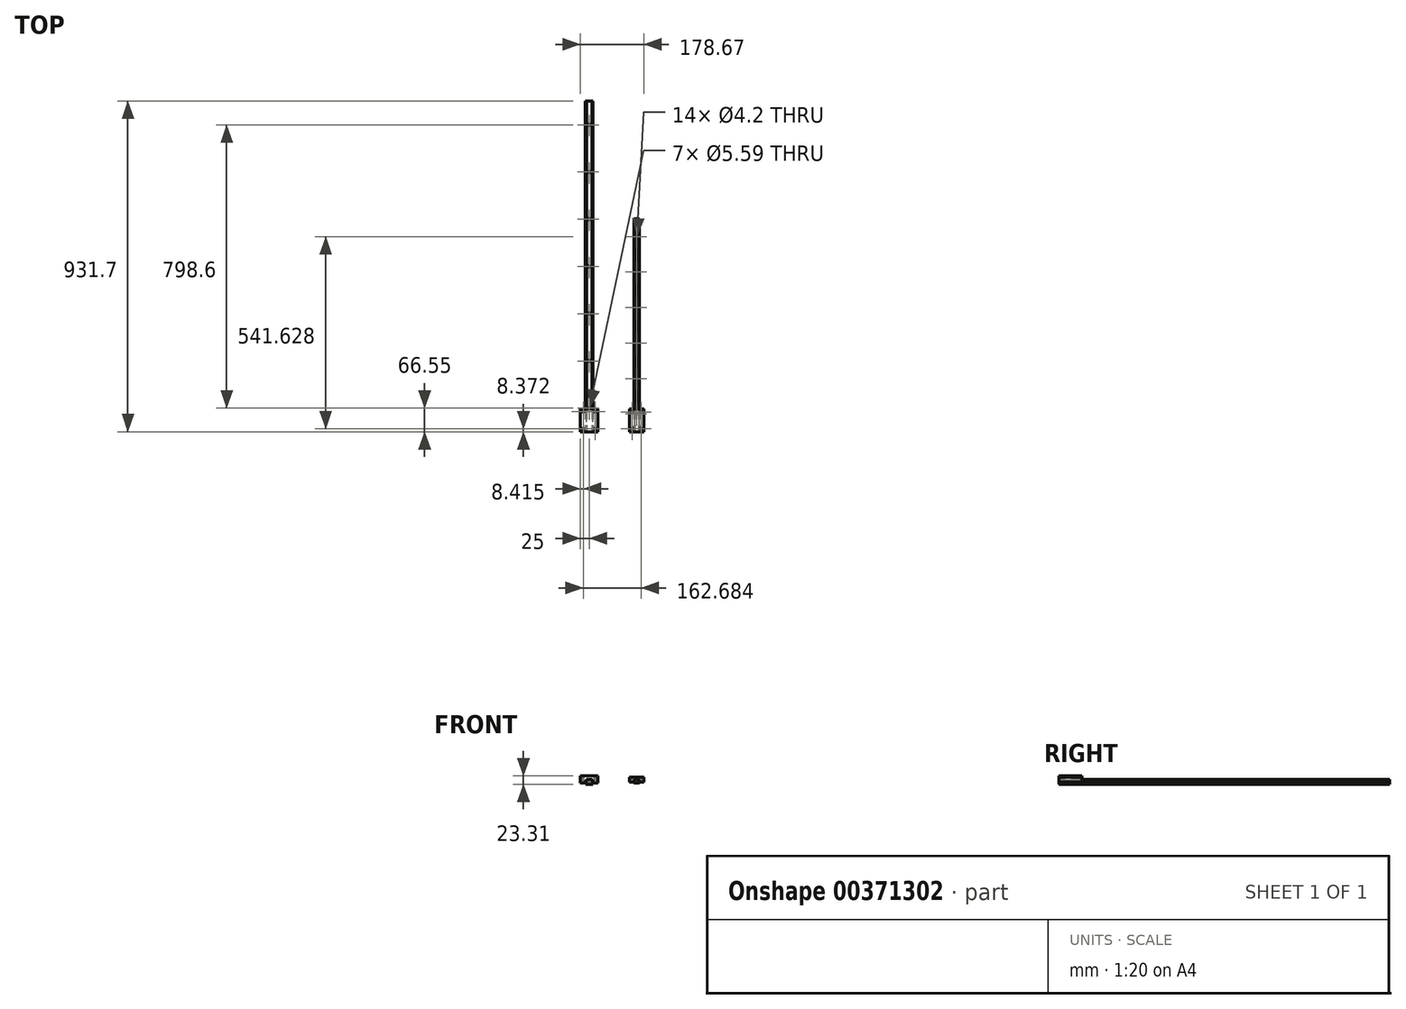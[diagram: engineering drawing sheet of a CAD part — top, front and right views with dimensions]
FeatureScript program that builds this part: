
annotation { "Feature Type Name" : "Feature", "Feature Type Description" : "" }
export const myFeature = defineFeature(function(context is Context, id is Id, definition is map)
    precondition{}
    {
        {
            var Q0;
            Q0=qCreatedBy(makeId("Front.planeOp"),FACE);
            var sketch = newSketch(context, id + "F0", { "sketchPlane" : qUnion([Q0])});
            skLineSegment(sketch, "E0", {"start": v(47.88, 76.41) * mm, "end": v(58.88, 76.41) * mm});
            skLineSegment(sketch, "E1", {"start": v(47.88, 76.41) * mm, "end": v(47.88, 75.41) * mm});
            skLineSegment(sketch, "E2", {"start": v(46.88, 74.41) * mm, "end": v(45.88, 74.41) * mm});
            skLineSegment(sketch, "E3", {"start": v(45.88, 74.41) * mm, "end": v(45.88, 73.91) * mm});
            skLineSegment(sketch, "E4", {"start": v(45.88, 73.91) * mm, "end": v(45.38, 73.91) * mm});
            skPoint(sketch, "E5.visualSharp", {"position": v(47.88, 74.41) * mm});
            skArc(sketch, "E5.filletArc", {"start": v(46.88, 74.41) * mm, "mid": v(47.59, 74.7) * mm, "end": v(47.88, 75.41) * mm});
            skLineSegment(sketch, "E6", {"start": v(45.38, 73.91) * mm, "end": v(45.38, 73.41) * mm});
            skLineSegment(sketch, "E7", {"start": v(45.38, 73.41) * mm, "end": v(45.88, 73.41) * mm});
            skLineSegment(sketch, "E8", {"start": v(45.88, 69.41) * mm, "end": v(45.88, 66.41) * mm});
            skArc(sketch, "E9", {"start": v(45.88, 69.41) * mm, "mid": v(46.83, 71.41) * mm, "end": v(45.88, 73.41) * mm});
            skLineSegment(sketch, "E10", {"start": v(53.38, 80.8) * mm, "end": v(53.38, 84.76) * mm, "construction": true});
            skPoint(sketch, "E10.startSnap0", {"position": v(53.38, 76.41) * mm});
            skLineSegment(sketch, "E11.MirrorCS", {"start": v(58.88, 76.41) * mm, "end": v(58.88, 75.41) * mm});
            skArc(sketch, "E12.MirrorCS", {"start": v(59.88, 74.41) * mm, "mid": v(59.17, 74.7) * mm, "end": v(58.88, 75.41) * mm});
            skLineSegment(sketch, "E13.MirrorCS", {"start": v(59.88, 74.41) * mm, "end": v(60.88, 74.41) * mm});
            skLineSegment(sketch, "E14.MirrorCS", {"start": v(60.88, 74.41) * mm, "end": v(60.88, 73.91) * mm});
            skLineSegment(sketch, "E15.MirrorCS", {"start": v(60.88, 73.91) * mm, "end": v(61.38, 73.91) * mm});
            skLineSegment(sketch, "E16.MirrorCS", {"start": v(61.38, 73.91) * mm, "end": v(61.38, 73.41) * mm});
            skLineSegment(sketch, "E17.MirrorCS", {"start": v(61.38, 73.41) * mm, "end": v(60.88, 73.41) * mm});
            skArc(sketch, "E18.MirrorCS", {"start": v(60.88, 69.41) * mm, "mid": v(59.93, 71.41) * mm, "end": v(60.88, 73.41) * mm});
            skLineSegment(sketch, "E19.MirrorCS", {"start": v(60.88, 69.41) * mm, "end": v(60.88, 66.41) * mm});
            skLineSegment(sketch, "E20", {"start": v(45.88, 66.41) * mm, "end": v(60.88, 66.41) * mm});
            skLineSegment(sketch, "E21", {"start": v(120.22, 88.93) * mm, "end": v(120.22, 157.33) * mm, "construction": true});
            skLineSegment(sketch, "E22.MirrorCS", {"start": v(194.55, 73.91) * mm, "end": v(195.05, 73.91) * mm});
            skLineSegment(sketch, "E23.MirrorCS", {"start": v(194.55, 74.41) * mm, "end": v(194.55, 73.91) * mm});
            skArc(sketch, "E24.MirrorCS", {"start": v(193.55, 74.41) * mm, "mid": v(192.85, 74.7) * mm, "end": v(192.55, 75.41) * mm});
            skLineSegment(sketch, "E25.MirrorCS", {"start": v(195.05, 73.41) * mm, "end": v(194.55, 73.41) * mm});
            skLineSegment(sketch, "E26.MirrorCS", {"start": v(179.55, 74.41) * mm, "end": v(179.55, 73.91) * mm});
            skLineSegment(sketch, "E27.MirrorCS", {"start": v(179.55, 73.91) * mm, "end": v(179.05, 73.91) * mm});
            skLineSegment(sketch, "E28.MirrorCS", {"start": v(193.55, 74.41) * mm, "end": v(194.55, 74.41) * mm});
            skLineSegment(sketch, "E29.MirrorCS", {"start": v(195.05, 73.91) * mm, "end": v(195.05, 73.41) * mm});
            skArc(sketch, "E30.MirrorCS", {"start": v(180.55, 74.41) * mm, "mid": v(181.26, 74.7) * mm, "end": v(181.55, 75.41) * mm});
            skLineSegment(sketch, "E31.MirrorCS", {"start": v(180.55, 74.41) * mm, "end": v(179.55, 74.41) * mm});
            skLineSegment(sketch, "E32.MirrorCS", {"start": v(179.05, 73.41) * mm, "end": v(179.55, 73.41) * mm});
            skLineSegment(sketch, "E33.MirrorCS", {"start": v(192.55, 76.41) * mm, "end": v(192.55, 75.41) * mm});
            skLineSegment(sketch, "E34.MirrorCS", {"start": v(179.05, 73.91) * mm, "end": v(179.05, 73.41) * mm});
            skLineSegment(sketch, "E35.MirrorCS", {"start": v(181.55, 76.41) * mm, "end": v(181.55, 75.41) * mm});
            skArc(sketch, "E36.MirrorCS", {"start": v(194.55, 69.41) * mm, "mid": v(193.6, 71.41) * mm, "end": v(194.55, 73.41) * mm});
            skArc(sketch, "E37.MirrorCS", {"start": v(179.55, 69.41) * mm, "mid": v(180.5, 71.41) * mm, "end": v(179.55, 73.41) * mm});
            skLineSegment(sketch, "E38.MirrorCS", {"start": v(179.55, 69.41) * mm, "end": v(179.55, 66.41) * mm});
            skLineSegment(sketch, "E39.MirrorCS", {"start": v(194.55, 69.41) * mm, "end": v(194.55, 66.41) * mm});
            skLineSegment(sketch, "E40.MirrorCS", {"start": v(192.55, 76.41) * mm, "end": v(181.55, 76.41) * mm});
            skLineSegment(sketch, "E41.MirrorCS", {"start": v(187.05, 80.8) * mm, "end": v(187.05, 84.76) * mm, "construction": true});
            skPoint(sketch, "E42.MirrorP", {"position": v(192.55, 74.41) * mm});
            skPoint(sketch, "E43.MirrorP", {"position": v(187.05, 76.41) * mm});
            skLineSegment(sketch, "E44.MirrorCS", {"start": v(194.55, 66.41) * mm, "end": v(179.55, 66.41) * mm});
            skSolve(sketch);
        }
        {
            var Q0;
            Q0=makeQuery(id+"F0.imprint","IMPRINT",FACE,{"disambiguationData":[TD([[makeQuery(id+"F0.imprint","IMPRINT",EDGE,{"derivedFrom":sQuery(id+"F0.wireOp",EDGE,"E0")}),-1.0]])]});
            extrude(context, id + "F1", {"entities" : qUnion([Q0]), "oppositeDirection" : true, "depth" : 700 * mm});
        }
        {
            var Q0;
            Q0=makeQuery(id+"F0.imprint","IMPRINT",FACE,{"disambiguationData":[TD([[makeQuery(id+"F0.imprint","IMPRINT",EDGE,{"derivedFrom":sQuery(id+"F0.wireOp",EDGE,"E22.MirrorCS")}),-1.0]])]});
            extrude(context, id + "F2", {"entities" : qUnion([Q0]), "oppositeDirection" : true, "depth" : 600 * mm});
        }
        {
            var Q0;
            Q0=makeQuery(id+"F1.opExtrude","SWEPT_FACE",FACE,{"disambiguationData":[OSD([sQuery(id+"F0.wireOp",EDGE,"E0")])]});
            var sketch = newSketch(context, id + "F3", { "sketchPlane" : qUnion([Q0])});
            skPoint(sketch, "E45", {"position": v(53.38, 50) * mm});
            skPoint(sketch, "E45.positionSnap0", {"position": v(53.38, 0) * mm});
            skPoint(sketch, "E46.0.1.0", {"position": v(53.38, 150) * mm});
            skPoint(sketch, "E46.0.2.0", {"position": v(53.38, 250) * mm});
            skPoint(sketch, "E46.0.3.0", {"position": v(53.38, 350) * mm});
            skPoint(sketch, "E46.0.4.0", {"position": v(53.38, 450) * mm});
            skPoint(sketch, "E46.0.5.0", {"position": v(53.38, 550) * mm});
            skPoint(sketch, "E46.0.6.0", {"position": v(53.38, 650) * mm});
            skPoint(sketch, "E46.0.7.0", {"position": v(53.38, 750) * mm});
            skPoint(sketch, "E46.0.8.0", {"position": v(53.38, 850) * mm});
            skPoint(sketch, "E46.0.9.0", {"position": v(53.38, 950) * mm});
            skPoint(sketch, "E46.1.0.0", {"position": v(187.05, 50) * mm});
            skPoint(sketch, "E46.1.1.0", {"position": v(187.05, 150) * mm});
            skPoint(sketch, "E46.1.2.0", {"position": v(187.05, 250) * mm});
            skPoint(sketch, "E46.1.3.0", {"position": v(187.05, 350) * mm});
            skPoint(sketch, "E46.1.4.0", {"position": v(187.05, 450) * mm});
            skPoint(sketch, "E46.1.5.0", {"position": v(187.05, 550) * mm});
            skPoint(sketch, "E46.1.6.0", {"position": v(187.05, 650) * mm});
            skPoint(sketch, "E46.1.7.0", {"position": v(187.05, 750) * mm});
            skPoint(sketch, "E46.1.8.0", {"position": v(187.05, 850) * mm});
            skPoint(sketch, "E46.1.9.0", {"position": v(187.05, 950) * mm});
            skLineSegment(sketch, "E46.direction1", {"start": v(53.38, 50) * mm, "end": v(187.05, 50) * mm, "construction": true});
            skLineSegment(sketch, "E46.direction2", {"start": v(53.38, 50) * mm, "end": v(53.38, 150) * mm, "construction": true});
            skSolve(sketch);
        }
        {
            var Q0;
            Q0=sQuery(id+"F3.wireOp",VERTEX,"E45");
            var Q1;
            Q1=sQuery(id+"F3.wireOp",VERTEX,"E46.0.1.0");
            var Q2;
            Q2=sQuery(id+"F3.wireOp",VERTEX,"E46.0.2.0");
            var Q3;
            Q3=sQuery(id+"F3.wireOp",VERTEX,"E46.0.3.0");
            var Q4;
            Q4=sQuery(id+"F3.wireOp",VERTEX,"E46.0.4.0");
            var Q5;
            Q5=sQuery(id+"F3.wireOp",VERTEX,"E46.0.5.0");
            var Q6;
            Q6=sQuery(id+"F3.wireOp",VERTEX,"E46.0.6.0");
            var Q7;
            Q7=sQuery(id+"F3.wireOp",VERTEX,"E46.1.0.0");
            var Q8;
            Q8=sQuery(id+"F3.wireOp",VERTEX,"E46.1.1.0");
            var Q9;
            Q9=sQuery(id+"F3.wireOp",VERTEX,"E46.1.2.0");
            var Q10;
            Q10=sQuery(id+"F3.wireOp",VERTEX,"E46.1.3.0");
            var Q11;
            Q11=sQuery(id+"F3.wireOp",VERTEX,"E46.1.4.0");
            var Q12;
            Q12=sQuery(id+"F3.wireOp",VERTEX,"E46.1.5.0");
            var Q13;
            Q13=makeQuery(id+"F1.opExtrude","SWEPT_BODY",BODY,{"disambiguationData":[OSD([sQuery(id+"F0.wireOp",EDGE,"E0"),sQuery(id+"F0.wireOp",EDGE,"E1"),sQuery(id+"F0.wireOp",EDGE,"E2"),sQuery(id+"F0.wireOp",EDGE,"E3"),sQuery(id+"F0.wireOp",EDGE,"E4"),sQuery(id+"F0.wireOp",EDGE,"E5.filletArc"),sQuery(id+"F0.wireOp",EDGE,"E6"),sQuery(id+"F0.wireOp",EDGE,"E7"),sQuery(id+"F0.wireOp",EDGE,"E8"),sQuery(id+"F0.wireOp",EDGE,"E9"),sQuery(id+"F0.wireOp",EDGE,"E11.MirrorCS"),sQuery(id+"F0.wireOp",EDGE,"E12.MirrorCS"),sQuery(id+"F0.wireOp",EDGE,"E13.MirrorCS"),sQuery(id+"F0.wireOp",EDGE,"E14.MirrorCS"),sQuery(id+"F0.wireOp",EDGE,"E15.MirrorCS"),sQuery(id+"F0.wireOp",EDGE,"E16.MirrorCS"),sQuery(id+"F0.wireOp",EDGE,"E17.MirrorCS"),sQuery(id+"F0.wireOp",EDGE,"E18.MirrorCS"),sQuery(id+"F0.wireOp",EDGE,"E19.MirrorCS"),sQuery(id+"F0.wireOp",EDGE,"E20")])]});
            var Q14;
            Q14=makeQuery(id+"F2.opExtrude","SWEPT_BODY",BODY,{"disambiguationData":[OSD([sQuery(id+"F0.wireOp",EDGE,"E22.MirrorCS"),sQuery(id+"F0.wireOp",EDGE,"E23.MirrorCS"),sQuery(id+"F0.wireOp",EDGE,"E24.MirrorCS"),sQuery(id+"F0.wireOp",EDGE,"E25.MirrorCS"),sQuery(id+"F0.wireOp",EDGE,"E26.MirrorCS"),sQuery(id+"F0.wireOp",EDGE,"E27.MirrorCS"),sQuery(id+"F0.wireOp",EDGE,"E28.MirrorCS"),sQuery(id+"F0.wireOp",EDGE,"E29.MirrorCS"),sQuery(id+"F0.wireOp",EDGE,"E30.MirrorCS"),sQuery(id+"F0.wireOp",EDGE,"E31.MirrorCS"),sQuery(id+"F0.wireOp",EDGE,"E32.MirrorCS"),sQuery(id+"F0.wireOp",EDGE,"E33.MirrorCS"),sQuery(id+"F0.wireOp",EDGE,"E34.MirrorCS"),sQuery(id+"F0.wireOp",EDGE,"E35.MirrorCS"),sQuery(id+"F0.wireOp",EDGE,"E36.MirrorCS"),sQuery(id+"F0.wireOp",EDGE,"E37.MirrorCS"),sQuery(id+"F0.wireOp",EDGE,"E38.MirrorCS"),sQuery(id+"F0.wireOp",EDGE,"E39.MirrorCS"),sQuery(id+"F0.wireOp",EDGE,"E40.MirrorCS"),sQuery(id+"F0.wireOp",EDGE,"E44.MirrorCS")])]});
            hole(context, id + "F4", {"style" : HoleStyle.SIMPLE, "endStyle" : HoleEndStyle.BLIND, "standardTappedOrClearance" : lookupTablePath({ "standard" : "ISO", "engagement" : "75%", "pitch" : "0.8 mm", "size" : "M5", "type" : "Tapped" }), "standardBlindInLast" : lookupTablePath({ "standard" : "ISO", "engagement" : "75%", "pitch" : "0.8 mm", "size" : "M5", "type" : "Tapped" }), "holeDiameter" : 4.2 * mm, "showTappedDepth" : true, "holeDepth" : 11 * mm, "isTappedThrough" : true, "tappedDepth" : 8.6 * mm, "tapClearance" : 3, "locations" : qUnion([Q0, Q1, Q2, Q3, Q4, Q5, Q6, Q7, Q8, Q9, Q10, Q11, Q12]), "scope" : qUnion([Q13, Q14]), "majorDiameter" : 5 * mm});
        }
        {
            var Q0;
            Q0=makeQuery(id+"F1.opExtrude","SWEPT_BODY",BODY,{"disambiguationData":[OSD([sQuery(id+"F0.wireOp",EDGE,"E0"),sQuery(id+"F0.wireOp",EDGE,"E1"),sQuery(id+"F0.wireOp",EDGE,"E2"),sQuery(id+"F0.wireOp",EDGE,"E3"),sQuery(id+"F0.wireOp",EDGE,"E4"),sQuery(id+"F0.wireOp",EDGE,"E5.filletArc"),sQuery(id+"F0.wireOp",EDGE,"E6"),sQuery(id+"F0.wireOp",EDGE,"E7"),sQuery(id+"F0.wireOp",EDGE,"E8"),sQuery(id+"F0.wireOp",EDGE,"E9"),sQuery(id+"F0.wireOp",EDGE,"E11.MirrorCS"),sQuery(id+"F0.wireOp",EDGE,"E12.MirrorCS"),sQuery(id+"F0.wireOp",EDGE,"E13.MirrorCS"),sQuery(id+"F0.wireOp",EDGE,"E14.MirrorCS"),sQuery(id+"F0.wireOp",EDGE,"E15.MirrorCS"),sQuery(id+"F0.wireOp",EDGE,"E16.MirrorCS"),sQuery(id+"F0.wireOp",EDGE,"E17.MirrorCS"),sQuery(id+"F0.wireOp",EDGE,"E18.MirrorCS"),sQuery(id+"F0.wireOp",EDGE,"E19.MirrorCS"),sQuery(id+"F0.wireOp",EDGE,"E20")])]});
            var Q1;
            Q1=sQuery(id+"F0.wireOp",VERTEX,"E10.startSnap0");
            transform(context, id + "F5", {"entities" : qUnion([Q0]), "transformType" : TransformType.SCALE_UNIFORMLY, "scale" : 1.33, "scalePoint" : qUnion([Q1]), "makeCopy" : false});
        }
        {
            var Q0;
            Q0=makeQuery(id+"F1.opExtrude","CAP_FACE",FACE,{"disambiguationData":[OSD([sQuery(id+"F0.wireOp",EDGE,"E0"),sQuery(id+"F0.wireOp",EDGE,"E1"),sQuery(id+"F0.wireOp",EDGE,"E2"),sQuery(id+"F0.wireOp",EDGE,"E3"),sQuery(id+"F0.wireOp",EDGE,"E4"),sQuery(id+"F0.wireOp",EDGE,"E5.filletArc"),sQuery(id+"F0.wireOp",EDGE,"E6"),sQuery(id+"F0.wireOp",EDGE,"E7"),sQuery(id+"F0.wireOp",EDGE,"E8"),sQuery(id+"F0.wireOp",EDGE,"E9"),sQuery(id+"F0.wireOp",EDGE,"E11.MirrorCS"),sQuery(id+"F0.wireOp",EDGE,"E12.MirrorCS"),sQuery(id+"F0.wireOp",EDGE,"E13.MirrorCS"),sQuery(id+"F0.wireOp",EDGE,"E14.MirrorCS"),sQuery(id+"F0.wireOp",EDGE,"E15.MirrorCS"),sQuery(id+"F0.wireOp",EDGE,"E16.MirrorCS"),sQuery(id+"F0.wireOp",EDGE,"E17.MirrorCS"),sQuery(id+"F0.wireOp",EDGE,"E18.MirrorCS"),sQuery(id+"F0.wireOp",EDGE,"E19.MirrorCS"),sQuery(id+"F0.wireOp",EDGE,"E20")])],"isStart":true});
            var sketch = newSketch(context, id + "F6", { "sketchPlane" : qUnion([Q0])});
            skLineSegment(sketch, "E47", {"start": v(43.4, 63.1) * mm, "end": v(63.36, 63.1) * mm});
            skSolve(sketch);
        }
        {
            var Q0;
            Q0=qCreatedBy(makeId("Front.planeOp"),FACE);
            var sketch = newSketch(context, id + "F7", { "sketchPlane" : qUnion([Q0])});
            skLineSegment(sketch, "E48.bottom", {"start": v(78.38, 86.41) * mm, "end": v(28.38, 86.41) * mm});
            skLineSegment(sketch, "E48.top", {"start": v(78.38, 66.1) * mm, "end": v(28.38, 66.1) * mm});
            skLineSegment(sketch, "E48.left", {"start": v(78.38, 86.41) * mm, "end": v(78.38, 66.1) * mm});
            skLineSegment(sketch, "E48.right", {"start": v(28.38, 86.41) * mm, "end": v(28.38, 66.1) * mm});
            skPoint(sketch, "E48.middle", {"position": v(53.38, 76.26) * mm});
            skLineSegment(sketch, "E49.0", {"start": v(47.88, 76.41) * mm, "end": v(58.88, 76.41) * mm});
            skLineSegment(sketch, "E50.0", {"start": v(46.06, 76.41) * mm, "end": v(60.7, 76.41) * mm});
            skLineSegment(sketch, "E51.0", {"start": v(46.06, 76.41) * mm, "end": v(46.06, 75.08) * mm});
            skArc(sketch, "E52.0", {"start": v(44.73, 73.75) * mm, "mid": v(45.67, 74.14) * mm, "end": v(46.06, 75.08) * mm});
            skLineSegment(sketch, "E53.0", {"start": v(44.73, 73.75) * mm, "end": v(43.4, 73.75) * mm});
            skPoint(sketch, "E54.0", {"position": v(43.4, 73.42) * mm});
            skLineSegment(sketch, "E55.0", {"start": v(43.4, 73.09) * mm, "end": v(42.73, 73.09) * mm});
            skLineSegment(sketch, "E56.0", {"start": v(43.4, 73.75) * mm, "end": v(43.4, 73.09) * mm});
            skLineSegment(sketch, "E57.0", {"start": v(42.73, 72.42) * mm, "end": v(43.4, 72.42) * mm});
            skPoint(sketch, "E58.0", {"position": v(42.73, 72.75) * mm});
            skArc(sketch, "E59.0", {"start": v(43.4, 67.1) * mm, "mid": v(44.66, 69.76) * mm, "end": v(43.4, 72.42) * mm});
            skLineSegment(sketch, "E60.0", {"start": v(42.73, 73.09) * mm, "end": v(42.73, 72.42) * mm});
            skLineSegment(sketch, "E61.0", {"start": v(43.4, 67.1) * mm, "end": v(43.4, 63.1) * mm});
            skLineSegment(sketch, "E62.0", {"start": v(63.36, 67.1) * mm, "end": v(63.36, 63.1) * mm});
            skArc(sketch, "E63.0", {"start": v(63.36, 67.1) * mm, "mid": v(62.1, 69.76) * mm, "end": v(63.36, 72.42) * mm});
            skLineSegment(sketch, "E64.0", {"start": v(64.03, 72.42) * mm, "end": v(63.36, 72.42) * mm});
            skLineSegment(sketch, "E65.0", {"start": v(64.03, 73.09) * mm, "end": v(64.03, 72.42) * mm});
            skLineSegment(sketch, "E66.0", {"start": v(63.36, 73.09) * mm, "end": v(64.03, 73.09) * mm});
            skLineSegment(sketch, "E67.0", {"start": v(63.36, 73.75) * mm, "end": v(63.36, 73.09) * mm});
            skLineSegment(sketch, "E68.0", {"start": v(62.03, 73.75) * mm, "end": v(63.36, 73.75) * mm});
            skArc(sketch, "E69.0", {"start": v(62.03, 73.75) * mm, "mid": v(61.1, 74.14) * mm, "end": v(60.7, 75.08) * mm});
            skLineSegment(sketch, "E70.0", {"start": v(60.7, 76.41) * mm, "end": v(60.7, 75.08) * mm});
            skLineSegment(sketch, "E71.bottom", {"start": v(207.05, 69.41) * mm, "end": v(167.05, 69.41) * mm});
            skLineSegment(sketch, "E71.top", {"start": v(207.05, 83.41) * mm, "end": v(167.05, 83.41) * mm});
            skLineSegment(sketch, "E71.left", {"start": v(207.05, 69.41) * mm, "end": v(207.05, 83.41) * mm});
            skLineSegment(sketch, "E71.right", {"start": v(167.05, 69.41) * mm, "end": v(167.05, 83.41) * mm});
            skPoint(sketch, "E71.middle", {"position": v(187.05, 76.41) * mm});
            skLineSegment(sketch, "E72.0", {"start": v(43.4, 63.1) * mm, "end": v(63.36, 63.1) * mm});
            skLineSegment(sketch, "E73.0", {"start": v(192.55, 76.41) * mm, "end": v(181.55, 76.41) * mm});
            skLineSegment(sketch, "E74.0", {"start": v(181.55, 76.41) * mm, "end": v(181.55, 75.41) * mm});
            skArc(sketch, "E75.0", {"start": v(180.55, 74.41) * mm, "mid": v(181.26, 74.7) * mm, "end": v(181.55, 75.41) * mm});
            skLineSegment(sketch, "E76.0", {"start": v(180.55, 74.41) * mm, "end": v(179.55, 74.41) * mm});
            skPoint(sketch, "E77.0", {"position": v(179.55, 74.16) * mm});
            skLineSegment(sketch, "E78.0", {"start": v(179.55, 74.41) * mm, "end": v(179.55, 73.91) * mm});
            skLineSegment(sketch, "E79.0", {"start": v(179.55, 73.91) * mm, "end": v(179.05, 73.91) * mm});
            skLineSegment(sketch, "E80.0", {"start": v(179.05, 73.41) * mm, "end": v(179.55, 73.41) * mm});
            skLineSegment(sketch, "E81.0", {"start": v(179.05, 73.91) * mm, "end": v(179.05, 73.41) * mm});
            skArc(sketch, "E82.0", {"start": v(179.55, 69.41) * mm, "mid": v(180.5, 71.41) * mm, "end": v(179.55, 73.41) * mm});
            skLineSegment(sketch, "E83.0", {"start": v(192.55, 76.41) * mm, "end": v(192.55, 75.41) * mm});
            skArc(sketch, "E84.0", {"start": v(193.55, 74.41) * mm, "mid": v(192.85, 74.7) * mm, "end": v(192.55, 75.41) * mm});
            skLineSegment(sketch, "E85.0", {"start": v(193.55, 74.41) * mm, "end": v(194.55, 74.41) * mm});
            skLineSegment(sketch, "E86.0", {"start": v(194.55, 74.41) * mm, "end": v(194.55, 73.91) * mm});
            skLineSegment(sketch, "E87.0", {"start": v(194.55, 73.91) * mm, "end": v(195.05, 73.91) * mm});
            skLineSegment(sketch, "E88.0", {"start": v(195.05, 73.91) * mm, "end": v(195.05, 73.41) * mm});
            skLineSegment(sketch, "E89.0", {"start": v(195.05, 73.41) * mm, "end": v(194.55, 73.41) * mm});
            skArc(sketch, "E90.0", {"start": v(194.55, 69.41) * mm, "mid": v(193.6, 71.41) * mm, "end": v(194.55, 73.41) * mm});
            skSolve(sketch);
        }
        {
            var Q0;
            Q0=makeQuery(id+"F7.imprint","IMPRINT",FACE,{"disambiguationData":[TD([[makeQuery(id+"F7.imprint","IMPRINT",EDGE,{"derivedFrom":sQuery(id+"F7.wireOp",EDGE,"E48.bottom")}),1.0]])]});
            var Q1;
            Q1=makeQuery(id+"F7.imprint","IMPRINT",FACE,{"disambiguationData":[TD([[makeQuery(id+"F7.imprint","IMPRINT",EDGE,{"derivedFrom":sQuery(id+"F7.wireOp",EDGE,"E71.top")}),1.0]])]});
            extrude(context, id + "F8", {"entities" : qUnion([Q0, Q1]), "oppositeDirection" : true, "depth" : 65 * mm});
        }
        {
            var Q0;
            Q0=makeQuery(id+"F8.opExtrude","SWEPT_FACE",FACE,{"disambiguationData":[OSD([sQuery(id+"F7.wireOp",EDGE,"E48.bottom")])]});
            var sketch = newSketch(context, id + "F9", { "sketchPlane" : qUnion([Q0])});
            skLineSegment(sketch, "E91.bottom", {"start": v(69.96, 56.63) * mm, "end": v(36.8, 56.63) * mm, "construction": true});
            skLineSegment(sketch, "E91.top", {"start": v(69.96, 8.37) * mm, "end": v(36.8, 8.37) * mm, "construction": true});
            skLineSegment(sketch, "E91.left", {"start": v(69.96, 56.63) * mm, "end": v(69.96, 8.37) * mm, "construction": true});
            skLineSegment(sketch, "E91.right", {"start": v(36.8, 56.63) * mm, "end": v(36.8, 8.37) * mm, "construction": true});
            skPoint(sketch, "E91.middle", {"position": v(53.38, 32.5) * mm});
            skPoint(sketch, "E91.middle.positionSnap0", {"position": v(28.38, 32.5) * mm});
            skPoint(sketch, "E91.middle.positionSnap1", {"position": v(53.38, 65) * mm});
            skPoint(sketch, "E91.centerSnap0", {"position": v(28.38, 32.5) * mm});
            skPoint(sketch, "E91.centerSnap1", {"position": v(53.38, 65) * mm});
            skPoint(sketch, "E92", {"position": v(187.05, 65) * mm});
            skPoint(sketch, "E93", {"position": v(187.05, 32.5) * mm});
            skPoint(sketch, "E94", {"position": v(167.05, 32.5) * mm});
            skLineSegment(sketch, "E95.bottom", {"start": v(199.48, 55.85) * mm, "end": v(174.63, 55.85) * mm, "construction": true});
            skLineSegment(sketch, "E95.top", {"start": v(199.48, 9.15) * mm, "end": v(174.63, 9.15) * mm, "construction": true});
            skLineSegment(sketch, "E95.left", {"start": v(199.48, 55.85) * mm, "end": v(199.48, 9.15) * mm, "construction": true});
            skLineSegment(sketch, "E95.right", {"start": v(174.63, 55.85) * mm, "end": v(174.63, 9.15) * mm, "construction": true});
            skSolve(sketch);
        }
        {
            var Q0;
            Q0=sQuery(id+"F9.wireOp",VERTEX,"E91.right.start");
            var Q1;
            Q1=sQuery(id+"F9.wireOp",VERTEX,"E91.bottom.start");
            var Q2;
            Q2=sQuery(id+"F9.wireOp",VERTEX,"E91.left.end");
            var Q3;
            Q3=sQuery(id+"F9.wireOp",VERTEX,"E91.top.end");
            var Q4;
            Q4=sQuery(id+"F9.wireOp",VERTEX,"E95.right.end");
            var Q5;
            Q5=sQuery(id+"F9.wireOp",VERTEX,"E95.left.end");
            var Q6;
            Q6=sQuery(id+"F9.wireOp",VERTEX,"E95.left.start");
            var Q7;
            Q7=sQuery(id+"F9.wireOp",VERTEX,"E95.right.start");
            var Q8;
            Q8=makeQuery(id+"F8.opExtrude","SWEPT_BODY",BODY,{"disambiguationData":[OSD([sQuery(id+"F7.wireOp",EDGE,"E48.bottom"),sQuery(id+"F7.wireOp",EDGE,"E48.top"),sQuery(id+"F7.wireOp",EDGE,"E48.left"),sQuery(id+"F7.wireOp",EDGE,"E48.right"),sQuery(id+"F7.wireOp",EDGE,"E50.0"),sQuery(id+"F7.wireOp",EDGE,"E51.0"),sQuery(id+"F7.wireOp",EDGE,"E52.0"),sQuery(id+"F7.wireOp",EDGE,"E53.0"),sQuery(id+"F7.wireOp",EDGE,"E55.0"),sQuery(id+"F7.wireOp",EDGE,"E56.0"),sQuery(id+"F7.wireOp",EDGE,"E57.0"),sQuery(id+"F7.wireOp",EDGE,"E59.0"),sQuery(id+"F7.wireOp",EDGE,"E60.0"),sQuery(id+"F7.wireOp",EDGE,"E61.0"),sQuery(id+"F7.wireOp",EDGE,"E62.0"),sQuery(id+"F7.wireOp",EDGE,"E63.0"),sQuery(id+"F7.wireOp",EDGE,"E64.0"),sQuery(id+"F7.wireOp",EDGE,"E65.0"),sQuery(id+"F7.wireOp",EDGE,"E66.0"),sQuery(id+"F7.wireOp",EDGE,"E67.0"),sQuery(id+"F7.wireOp",EDGE,"E68.0"),sQuery(id+"F7.wireOp",EDGE,"E69.0"),sQuery(id+"F7.wireOp",EDGE,"E70.0")])]});
            var Q9;
            Q9=makeQuery(id+"F8.opExtrude","SWEPT_BODY",BODY,{"disambiguationData":[OSD([sQuery(id+"F7.wireOp",EDGE,"E71.bottom"),sQuery(id+"F7.wireOp",EDGE,"E71.top"),sQuery(id+"F7.wireOp",EDGE,"E71.left"),sQuery(id+"F7.wireOp",EDGE,"E71.right"),sQuery(id+"F7.wireOp",EDGE,"E73.0"),sQuery(id+"F7.wireOp",EDGE,"E74.0"),sQuery(id+"F7.wireOp",EDGE,"E75.0"),sQuery(id+"F7.wireOp",EDGE,"E76.0"),sQuery(id+"F7.wireOp",EDGE,"E78.0"),sQuery(id+"F7.wireOp",EDGE,"E79.0"),sQuery(id+"F7.wireOp",EDGE,"E80.0"),sQuery(id+"F7.wireOp",EDGE,"E81.0"),sQuery(id+"F7.wireOp",EDGE,"E82.0"),sQuery(id+"F7.wireOp",EDGE,"E83.0"),sQuery(id+"F7.wireOp",EDGE,"E84.0"),sQuery(id+"F7.wireOp",EDGE,"E85.0"),sQuery(id+"F7.wireOp",EDGE,"E86.0"),sQuery(id+"F7.wireOp",EDGE,"E87.0"),sQuery(id+"F7.wireOp",EDGE,"E88.0"),sQuery(id+"F7.wireOp",EDGE,"E89.0"),sQuery(id+"F7.wireOp",EDGE,"E90.0")])]});
            hole(context, id + "F10", {"style" : HoleStyle.SIMPLE, "endStyle" : HoleEndStyle.BLIND, "standardTappedOrClearance" : lookupTablePath({ "standard" : "ISO", "engagement" : "75%", "pitch" : "0.8 mm", "size" : "M5", "type" : "Tapped" }), "standardBlindInLast" : lookupTablePath({ "standard" : "ISO", "engagement" : "75%", "pitch" : "0.8 mm", "size" : "M5", "type" : "Tapped" }), "holeDiameter" : 4.2 * mm, "showTappedDepth" : true, "holeDepth" : 20 * mm, "isTappedThrough" : true, "tappedDepth" : 17.6 * mm, "tapClearance" : 3, "locations" : qUnion([Q0, Q1, Q2, Q3, Q4, Q5, Q6, Q7]), "scope" : qUnion([Q8, Q9]), "majorDiameter" : 5 * mm});
        }
    });
